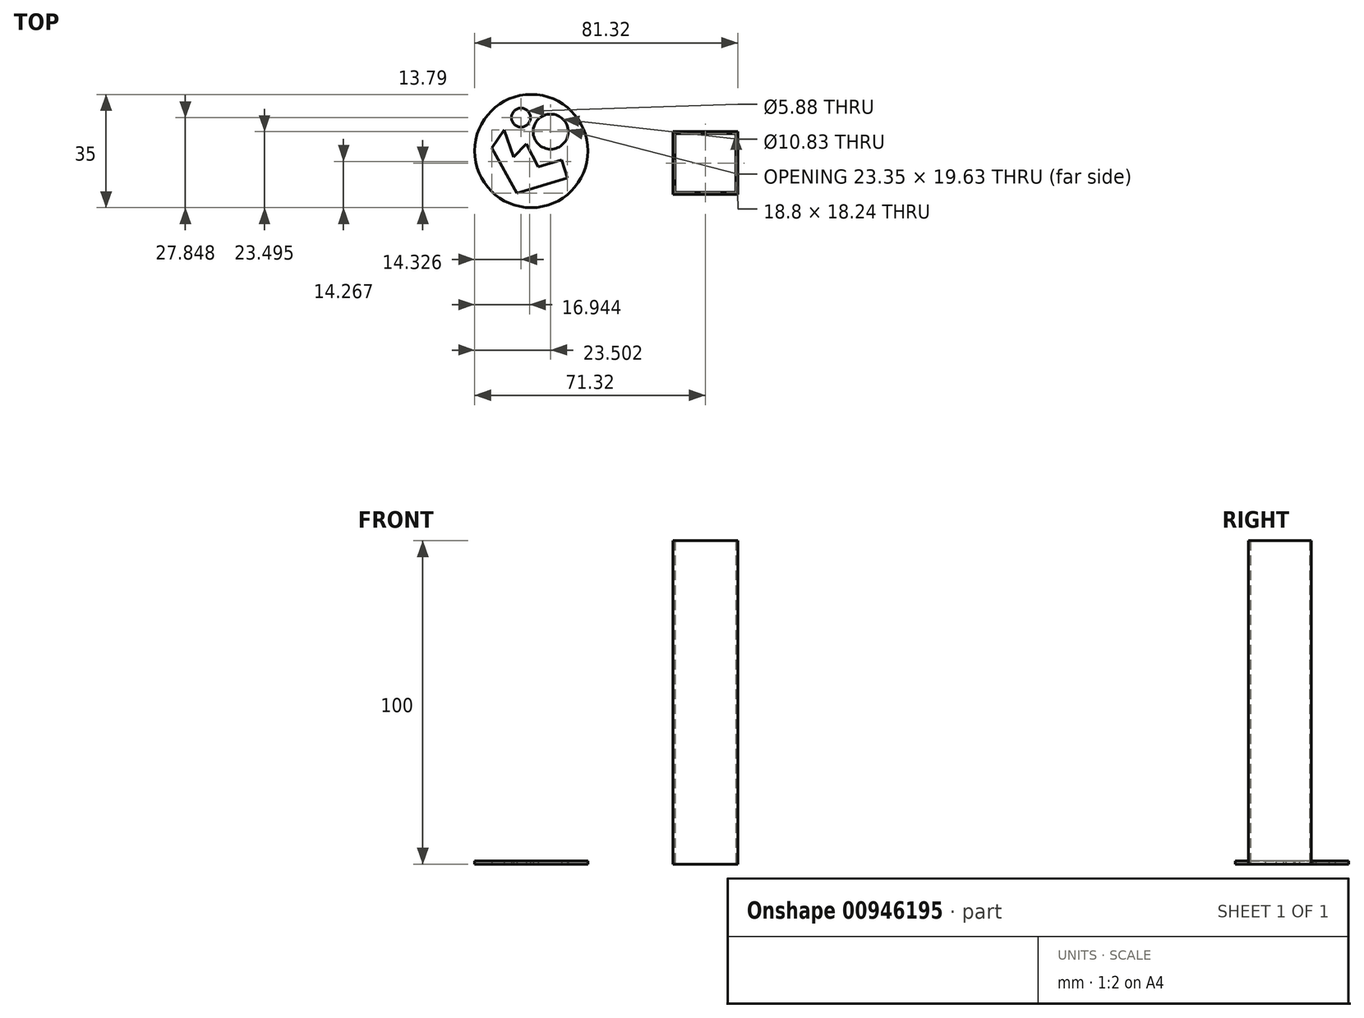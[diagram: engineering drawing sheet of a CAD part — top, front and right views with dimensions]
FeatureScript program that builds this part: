
annotation { "Feature Type Name" : "Feature", "Feature Type Description" : "" }
export const myFeature = defineFeature(function(context is Context, id is Id, definition is map)
    precondition{}
    {
        {
            var Q0;
            Q0=qCreatedBy(makeId("Top.planeOp"),FACE);
            var sketch = newSketch(context, id + "F0", { "sketchPlane" : qUnion([Q0])});
            skLineSegment(sketch, "E0.bottom", {"start": v(-10, 10) * mm, "end": v(10, 10) * mm});
            skLineSegment(sketch, "E0.top", {"start": v(-10, -9.44) * mm, "end": v(10, -9.44) * mm});
            skLineSegment(sketch, "E0.left", {"start": v(-10, 10) * mm, "end": v(-10, -9.44) * mm});
            skLineSegment(sketch, "E0.right", {"start": v(10, 10) * mm, "end": v(10, -9.44) * mm});
            skCircle(sketch, "E1", {"center": v(-53.82, 3.99) * mm, "radius": 17.5 * mm});
            skLineSegment(sketch, "E2", {"start": v(-66.05, 4.93) * mm, "end": v(-62.17, 10.57) * mm});
            skLineSegment(sketch, "E3", {"start": v(-62.17, 10.57) * mm, "end": v(-59.23, 2.1) * mm});
            skLineSegment(sketch, "E4", {"start": v(-59.23, 2.1) * mm, "end": v(-55.35, 6.22) * mm});
            skLineSegment(sketch, "E5", {"start": v(-55.35, 6.22) * mm, "end": v(-51.7, -0.95) * mm});
            skLineSegment(sketch, "E6", {"start": v(-51.7, -0.95) * mm, "end": v(-44.4, 1.28) * mm});
            skLineSegment(sketch, "E7", {"start": v(-44.4, 1.28) * mm, "end": v(-42.7, -4.29) * mm});
            skLineSegment(sketch, "E8", {"start": v(-42.7, -4.29) * mm, "end": v(-58.28, -9.06) * mm});
            skLineSegment(sketch, "E9", {"start": v(-58.28, -9.06) * mm, "end": v(-66.05, 4.93) * mm});
            skCircle(sketch, "E10", {"center": v(-57, 14.34) * mm, "radius": 2.94 * mm});
            skCircle(sketch, "E11", {"center": v(-47.82, 9.99) * mm, "radius": 5.42 * mm});
            skLineSegment(sketch, "E12.0", {"start": v(-9.4, -8.84) * mm, "end": v(9.4, -8.84) * mm});
            skLineSegment(sketch, "E12.1", {"start": v(-9.4, 9.4) * mm, "end": v(-9.4, -8.84) * mm});
            skLineSegment(sketch, "E12.2", {"start": v(-9.4, 9.4) * mm, "end": v(9.4, 9.4) * mm});
            skLineSegment(sketch, "E12.3", {"start": v(9.4, 9.4) * mm, "end": v(9.4, -8.84) * mm});
            skSolve(sketch);
        }
        {
            var Q0;
            Q0=makeQuery(id+"F0.imprint","IMPRINT",FACE,{"disambiguationData":[TD([[makeQuery(id+"F0.imprint","IMPRINT",EDGE,{"derivedFrom":sQuery(id+"F0.wireOp",EDGE,"E0.bottom")}),-1.0]])]});
            extrude(context, id + "F1", {"entities" : qUnion([Q0]), "depth" : 100 * mm, "offsetDistance" : 25 * mm});
        }
        {
            var Q0;
            Q0=makeQuery(id+"F0.imprint","IMPRINT",FACE,{"disambiguationData":[TD([[makeQuery(id+"F0.imprint","IMPRINT",EDGE,{"derivedFrom":sQuery(id+"F0.wireOp",EDGE,"E1")}),1.0]])]});
            extrude(context, id + "F2", {"entities" : qUnion([Q0]), "depth" : 1 * mm, "offsetDistance" : 25 * mm});
        }
    });
